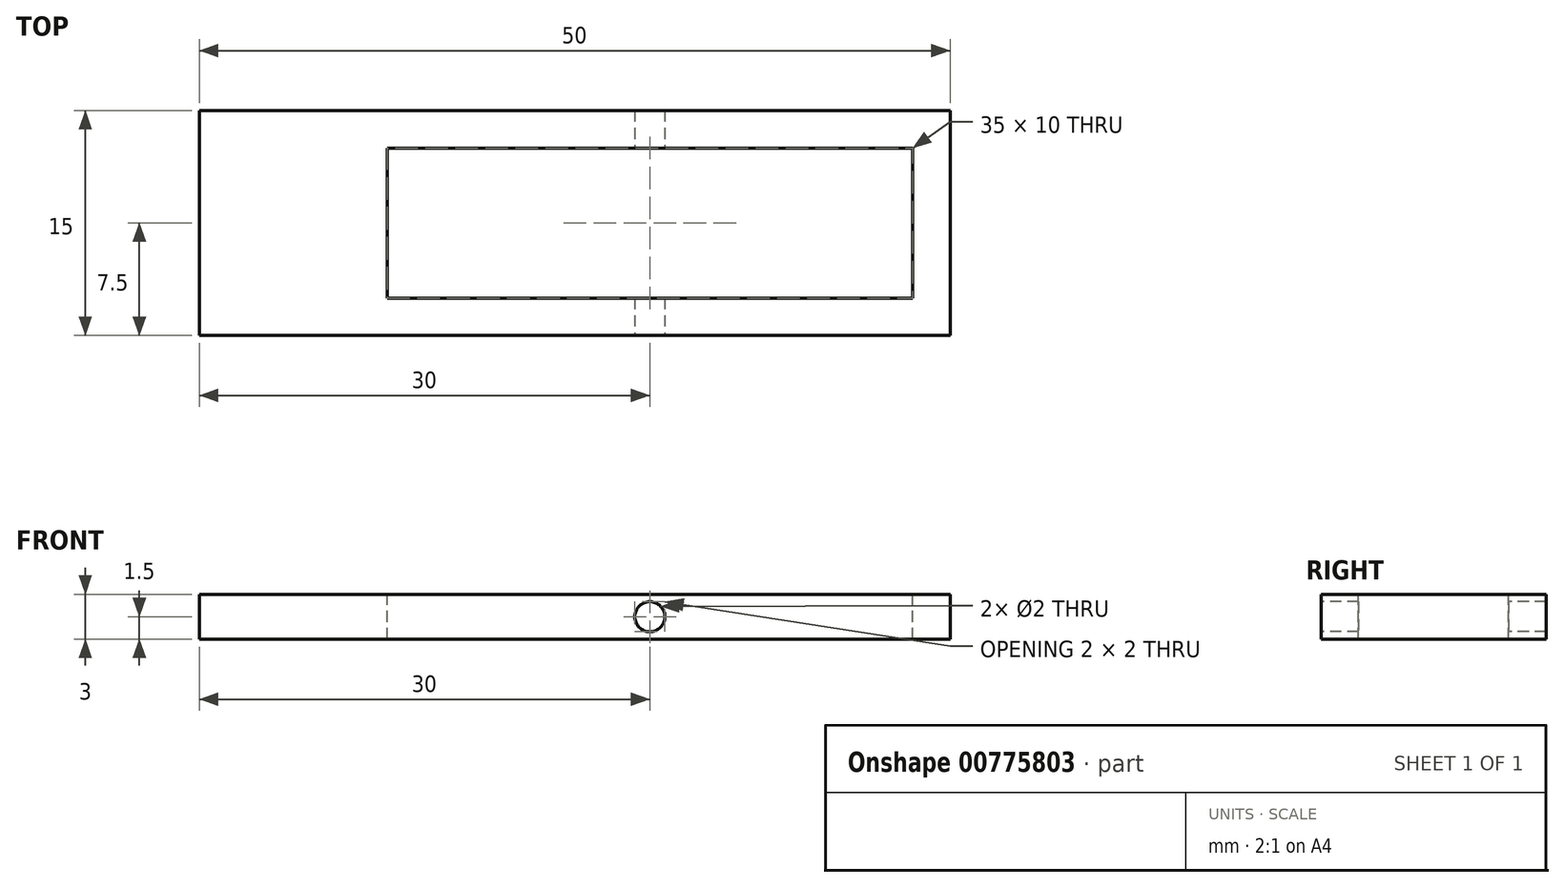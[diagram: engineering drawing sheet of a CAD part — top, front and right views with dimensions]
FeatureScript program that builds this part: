
annotation { "Feature Type Name" : "Feature", "Feature Type Description" : "" }
export const myFeature = defineFeature(function(context is Context, id is Id, definition is map)
    precondition{}
    {
        {
            var Q0;
            Q0=qCreatedBy(makeId("Front.planeOp"),FACE);
            var sketch = newSketch(context, id + "F0", { "sketchPlane" : qUnion([Q0])});
            skLineSegment(sketch, "E0.bottom", {"start": v(25, 1.5) * mm, "end": v(-25, 1.5) * mm});
            skLineSegment(sketch, "E0.top", {"start": v(25, -1.5) * mm, "end": v(-25, -1.5) * mm});
            skLineSegment(sketch, "E0.left", {"start": v(25, 1.5) * mm, "end": v(25, -1.5) * mm});
            skLineSegment(sketch, "E0.right", {"start": v(-25, 1.5) * mm, "end": v(-25, -1.5) * mm});
            skPoint(sketch, "E0.middle", {"position": v(0, 0) * mm});
            skPoint(sketch, "E1", {"position": v(5, 0) * mm});
            skSolve(sketch);
        }
        {
            var Q0;
            Q0=makeQuery(id+"F0.imprint","IMPRINT",FACE,{"disambiguationData":[TD([[makeQuery(id+"F0.imprint","IMPRINT",EDGE,{"derivedFrom":sQuery(id+"F0.wireOp",EDGE,"E0.bottom")}),1.0]])]});
            extrude(context, id + "F1", {"entities" : qUnion([Q0]), "endBound" : BoundingType.SYMMETRIC, "depth" : 15 * mm, "offsetDistance" : 25 * mm});
        }
        {
            var Q0;
            Q0=qCreatedBy(makeId("Top.planeOp"),FACE);
            var sketch = newSketch(context, id + "F2", { "sketchPlane" : qUnion([Q0])});
            skLineSegment(sketch, "E2.bottom", {"start": v(22.5, -5) * mm, "end": v(-12.5, -5) * mm});
            skLineSegment(sketch, "E2.top", {"start": v(22.5, 5) * mm, "end": v(-12.5, 5) * mm});
            skLineSegment(sketch, "E2.left", {"start": v(22.5, -5) * mm, "end": v(22.5, 5) * mm});
            skLineSegment(sketch, "E2.right", {"start": v(-12.5, -5) * mm, "end": v(-12.5, 5) * mm});
            skPoint(sketch, "E2.middle", {"position": v(5, 0) * mm});
            skSolve(sketch);
        }
        {
            var Q0;
            Q0 = qSketchRegion(id + "F2", true);
            extrude(context, id + "F3", {"entities" : qUnion([Q0]), "operationType" : NewBodyOperationType.REMOVE, "endBound" : BoundingType.SYMMETRIC, "oppositeDirection" : true, "depth" : 3 * mm, "offsetDistance" : 25 * mm});
        }
        {
            var Q0;
            Q0=makeQuery(id+"F1.opExtrude","CAP_FACE",FACE,{"disambiguationData":[OSD([sQuery(id+"F0.wireOp",EDGE,"E0.bottom"),sQuery(id+"F0.wireOp",EDGE,"E0.top"),sQuery(id+"F0.wireOp",EDGE,"E0.left"),sQuery(id+"F0.wireOp",EDGE,"E0.right")])],"isStart":false});
            var sketch = newSketch(context, id + "F4", { "sketchPlane" : qUnion([Q0])});
            skPoint(sketch, "E3", {"position": v(5, 0) * mm});
            skSolve(sketch);
        }
        {
            var Q0;
            Q0=sQuery(id+"F4.wireOp",VERTEX,"E3");
            var Q1;
            Q1=makeQuery(id+"F1.opExtrude","SWEPT_BODY",BODY,{"disambiguationData":[OSD([sQuery(id+"F0.wireOp",EDGE,"E0.bottom"),sQuery(id+"F0.wireOp",EDGE,"E0.top"),sQuery(id+"F0.wireOp",EDGE,"E0.left"),sQuery(id+"F0.wireOp",EDGE,"E0.right")])]});
            hole(context, id + "F5", {"style" : HoleStyle.SIMPLE, "endStyle" : HoleEndStyle.THROUGH, "holeDiameter" : 2 * mm, "majorDiameter" : 5 * mm, "isTappedThrough" : true, "tappedDepth" : 12 * mm, "tapClearance" : 3, "locations" : qUnion([Q0]), "scope" : qUnion([Q1])});
        }
    });
